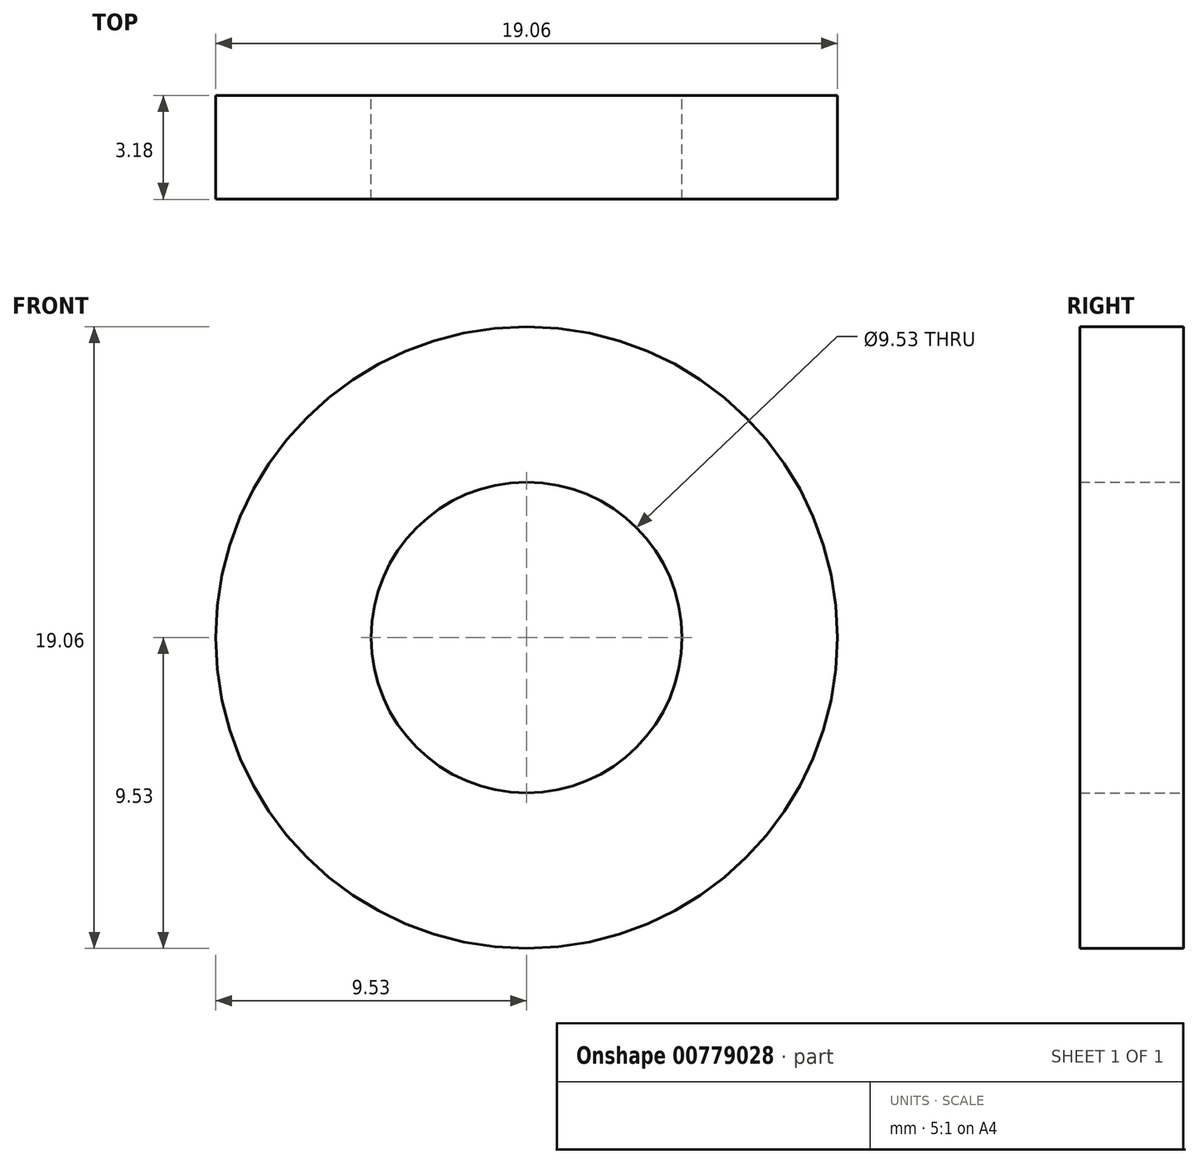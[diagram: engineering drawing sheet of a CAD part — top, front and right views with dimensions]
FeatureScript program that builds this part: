
annotation { "Feature Type Name" : "Feature", "Feature Type Description" : "" }
export const myFeature = defineFeature(function(context is Context, id is Id, definition is map)
    precondition{}
    {
        {
            var Q0;
            Q0=qCreatedBy(makeId("Front.planeOp"),FACE);
            var sketch = newSketch(context, id + "F0", { "sketchPlane" : qUnion([Q0])});
            skCircle(sketch, "E0", {"center": v(0, 0) * mm, "radius": 9.53 * mm});
            skCircle(sketch, "E1", {"center": v(0, 0) * mm, "radius": 4.76 * mm});
            skSolve(sketch);
        }
        {
            var Q0;
            Q0 = qSketchRegion(id + "F0", true);
            extrude(context, id + "F1", {"entities" : qUnion([Q0]), "depth" : 3.17 * mm, "offsetDistance" : 25.4 * mm});
        }
    });
